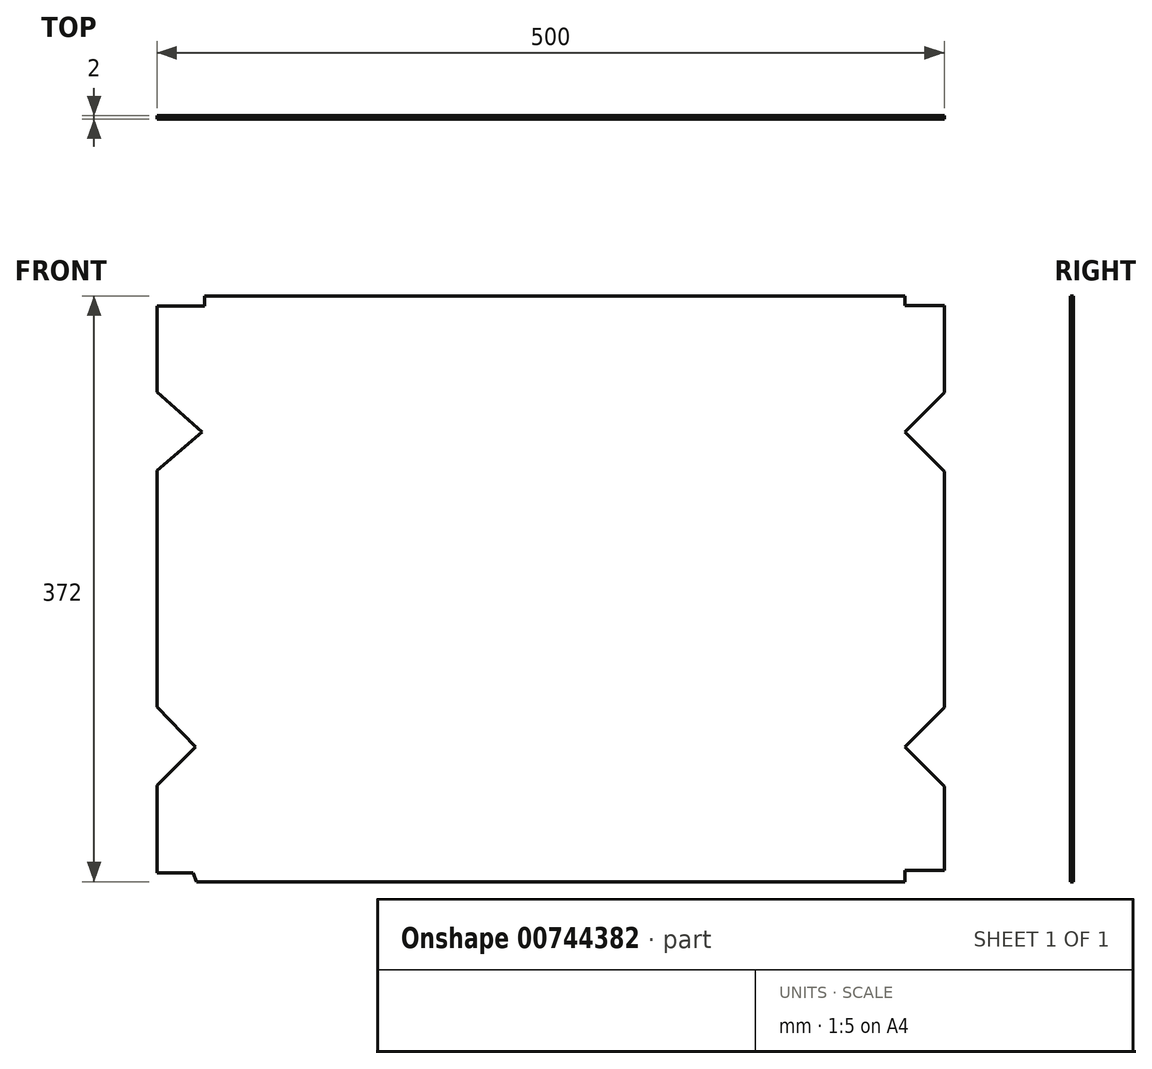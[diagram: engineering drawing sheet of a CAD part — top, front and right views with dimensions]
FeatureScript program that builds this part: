
annotation { "Feature Type Name" : "Feature", "Feature Type Description" : "" }
export const myFeature = defineFeature(function(context is Context, id is Id, definition is map)
    precondition{}
    {
        {
            var Q0;
            Q0=qCreatedBy(makeId("Front.planeOp"),FACE);
            var sketch = newSketch(context, id + "F0", { "sketchPlane" : qUnion([Q0])});
            skLineSegment(sketch, "E0.bottom", {"start": v(222.56, -181.1) * mm, "end": v(-227.44, -181.1) * mm});
            skLineSegment(sketch, "E0.top", {"start": v(222.56, 190.9) * mm, "end": v(-222.37, 190.9) * mm});
            skLineSegment(sketch, "E0.left", {"start": v(247.56, -174) * mm, "end": v(247.56, -120.48) * mm});
            skLineSegment(sketch, "E0.right", {"start": v(-252.44, -175.48) * mm, "end": v(-252.44, -120) * mm});
            skPoint(sketch, "E0.middle", {"position": v(0, 0) * mm});
            skLineSegment(sketch, "E1", {"start": v(-252.44, 184.52) * mm, "end": v(-252.44, 130.01) * mm});
            skLineSegment(sketch, "E2", {"start": v(-227.44, -181.1) * mm, "end": v(-229.54, -175.48) * mm});
            skLineSegment(sketch, "E3", {"start": v(-222.37, 190.9) * mm, "end": v(-222.37, 184.52) * mm});
            skLineSegment(sketch, "E4", {"start": v(-222.37, 184.52) * mm, "end": v(-252.44, 184.52) * mm});
            skLineSegment(sketch, "E5", {"start": v(-229.54, -175.48) * mm, "end": v(-252.44, -175.48) * mm});
            skLineSegment(sketch, "E6", {"start": v(-227.44, -181.1) * mm, "end": v(222.56, -181.1) * mm});
            skLineSegment(sketch, "E7", {"start": v(222.56, -181.1) * mm, "end": v(222.56, -180) * mm});
            skLineSegment(sketch, "E8", {"start": v(222.56, 184.9) * mm, "end": v(222.56, 190.9) * mm});
            skLineSegment(sketch, "E9", {"start": v(222.56, 184.9) * mm, "end": v(247.56, 184.9) * mm});
            skLineSegment(sketch, "E10", {"start": v(-223.96, 104.52) * mm, "end": v(222.56, 104.52) * mm});
            skLineSegment(sketch, "E11", {"start": v(-227.95, -95.48) * mm, "end": v(222.56, -95.48) * mm});
            skLineSegment(sketch, "E12", {"start": v(-222.37, 184.52) * mm, "end": v(-229.54, -175.48) * mm});
            skLineSegment(sketch, "E13", {"start": v(-223.96, 104.52) * mm, "end": v(-223.46, 129.47) * mm});
            skLineSegment(sketch, "E14", {"start": v(-252.44, 130.01) * mm, "end": v(-223.96, 104.52) * mm});
            skLineSegment(sketch, "E15", {"start": v(-223.96, 104.52) * mm, "end": v(-224.46, 79.48) * mm});
            skLineSegment(sketch, "E16", {"start": v(-252.44, 80.01) * mm, "end": v(-223.96, 104.52) * mm});
            skLineSegment(sketch, "E17", {"start": v(-227.95, -95.48) * mm, "end": v(-227.45, -70.49) * mm});
            skLineSegment(sketch, "E18", {"start": v(-227.95, -95.48) * mm, "end": v(-228.44, -120.48) * mm});
            skLineSegment(sketch, "E19", {"start": v(-227.95, -95.48) * mm, "end": v(-252.44, -120) * mm});
            skLineSegment(sketch, "E20", {"start": v(-227.95, -95.48) * mm, "end": v(-252.44, -69.99) * mm});
            skLineSegment(sketch, "E21.trimOffspring", {"start": v(-252.44, 80.01) * mm, "end": v(-252.44, -69.99) * mm});
            skLineSegment(sketch, "E22.trimOffspring", {"start": v(-252.44, 130.01) * mm, "end": v(-252.44, 190.9) * mm});
            skLineSegment(sketch, "E23.trimOffspring", {"start": v(-252.44, -69.99) * mm, "end": v(-252.44, -15.48) * mm});
            skLineSegment(sketch, "E24.trimOffspring", {"start": v(-252.44, -69.99) * mm, "end": v(-252.44, 80.01) * mm});
            skLineSegment(sketch, "E25", {"start": v(222.56, -180) * mm, "end": v(222.56, -174) * mm});
            skLineSegment(sketch, "E26", {"start": v(222.56, -174) * mm, "end": v(247.56, -174) * mm});
            skLineSegment(sketch, "E27", {"start": v(222.56, 184.9) * mm, "end": v(222.56, -174) * mm});
            skLineSegment(sketch, "E28", {"start": v(222.56, 104.52) * mm, "end": v(247.56, 129.52) * mm});
            skLineSegment(sketch, "E29", {"start": v(222.56, 104.52) * mm, "end": v(247.56, 79.52) * mm});
            skLineSegment(sketch, "E30.trimOffspring", {"start": v(247.56, 129.52) * mm, "end": v(247.56, 184.9) * mm});
            skLineSegment(sketch, "E31", {"start": v(247.56, -120.48) * mm, "end": v(222.56, -95.48) * mm});
            skLineSegment(sketch, "E32", {"start": v(222.56, -95.48) * mm, "end": v(247.56, -70.48) * mm});
            skLineSegment(sketch, "E33.trimOffspring", {"start": v(247.56, -70.48) * mm, "end": v(247.56, 79.52) * mm});
            skLineSegment(sketch, "E34", {"start": v(-229.54, -175.48) * mm, "end": v(-227.44, -181.1) * mm});
            skPoint(sketch, "E35.orphan", {"position": v(-252.44, -181.1) * mm});
            skSolve(sketch);
        }
        {
            var Q0;
            Q0 = qSketchRegion(id + "F0", true);
            extrude(context, id + "F1", {"entities" : qUnion([Q0]), "depth" : 2 * mm, "offsetDistance" : 25 * mm});
        }
    });
